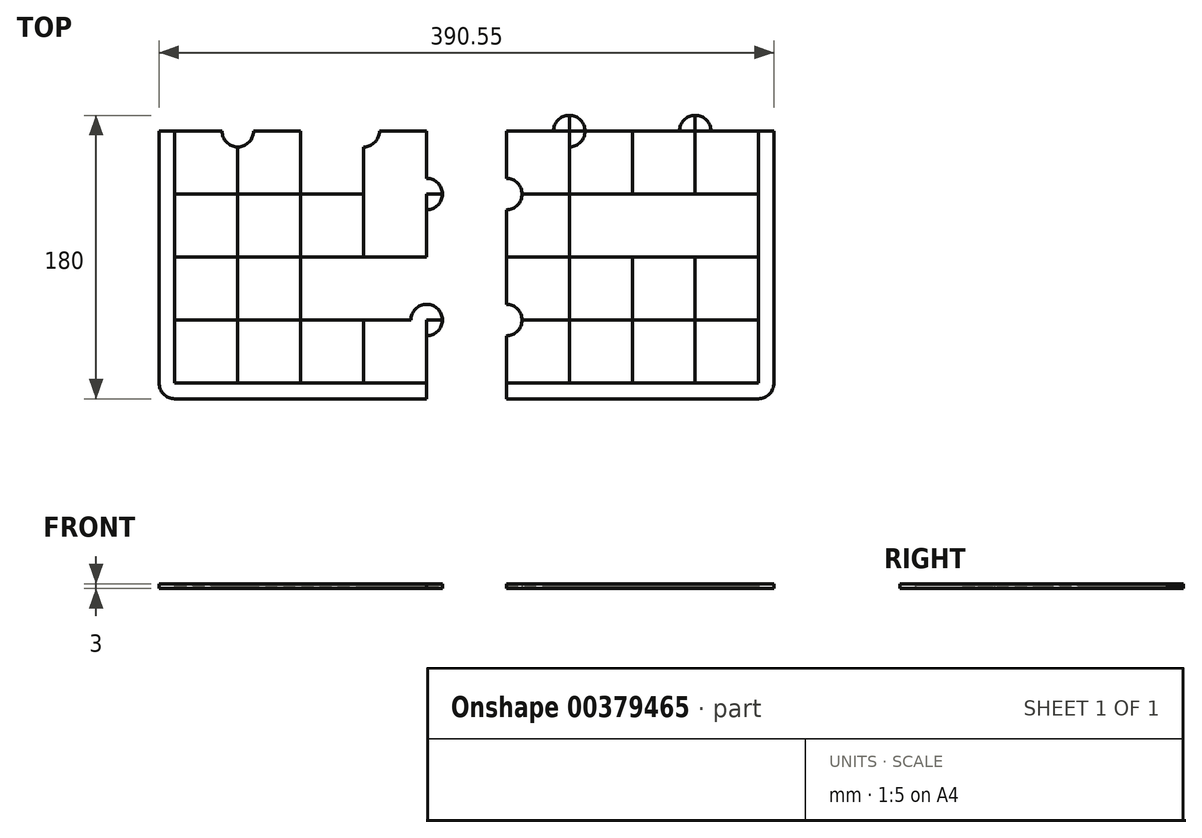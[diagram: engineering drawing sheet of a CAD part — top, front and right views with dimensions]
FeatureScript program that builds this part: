
annotation { "Feature Type Name" : "Feature", "Feature Type Description" : "" }
export const myFeature = defineFeature(function(context is Context, id is Id, definition is map)
    precondition{}
    {
        {
            var Q0;
            Q0=qCreatedBy(makeId("Top.planeOp"),FACE);
            var sketch = newSketch(context, id + "F0", { "sketchPlane" : qUnion([Q0])});
            skLineSegment(sketch, "E0.bottom", {"start": v(20, -20) * mm, "end": v(-20, -20) * mm});
            skLineSegment(sketch, "E0.top", {"start": v(20, 20) * mm, "end": v(-20, 20) * mm});
            skLineSegment(sketch, "E0.left", {"start": v(20, -20) * mm, "end": v(20, 20) * mm});
            skLineSegment(sketch, "E0.right", {"start": v(-20, -20) * mm, "end": v(-20, 20) * mm});
            skPoint(sketch, "E0.middle", {"position": v(0, 0) * mm});
            skLineSegment(sketch, "E1.bottom", {"start": v(-20, 20) * mm, "end": v(-60, 20) * mm});
            skLineSegment(sketch, "E1.top", {"start": v(-20, -20) * mm, "end": v(-60, -20) * mm});
            skLineSegment(sketch, "E1.left", {"start": v(-20, 20) * mm, "end": v(-20, -20) * mm});
            skLineSegment(sketch, "E1.right", {"start": v(-60, 20) * mm, "end": v(-60, -20) * mm});
            skLineSegment(sketch, "E2.bottom", {"start": v(20, -20) * mm, "end": v(60, -20) * mm});
            skLineSegment(sketch, "E2.top", {"start": v(20, 20) * mm, "end": v(60, 20) * mm});
            skLineSegment(sketch, "E2.right", {"start": v(60, -20) * mm, "end": v(60, 20) * mm});
            skLineSegment(sketch, "E3.bottom", {"start": v(-60, -20) * mm, "end": v(-100, -20) * mm});
            skLineSegment(sketch, "E3.top", {"start": v(-60, 20) * mm, "end": v(-100, 20) * mm});
            skLineSegment(sketch, "E3.left", {"start": v(-60, -20) * mm, "end": v(-60, 20) * mm});
            skLineSegment(sketch, "E3.right", {"start": v(-100, -20) * mm, "end": v(-100, 20) * mm});
            skLineSegment(sketch, "E4.bottom", {"start": v(-100, -20) * mm, "end": v(-60, -20) * mm});
            skLineSegment(sketch, "E4.top", {"start": v(-100, -60) * mm, "end": v(-60, -60) * mm});
            skLineSegment(sketch, "E4.left", {"start": v(-100, -20) * mm, "end": v(-100, -60) * mm});
            skLineSegment(sketch, "E4.right", {"start": v(-60, -20) * mm, "end": v(-60, -60) * mm});
            skLineSegment(sketch, "E5.top", {"start": v(-100, -100) * mm, "end": v(-60, -100) * mm});
            skLineSegment(sketch, "E5.left", {"start": v(-100, -60) * mm, "end": v(-100, -100) * mm});
            skLineSegment(sketch, "E5.right", {"start": v(-60, -60) * mm, "end": v(-60, -100) * mm});
            skPoint(sketch, "E6.oppositeSnap0", {"position": v(-60, -80) * mm});
            skLineSegment(sketch, "E6.top", {"start": v(-100, -140) * mm, "end": v(-60, -140) * mm});
            skLineSegment(sketch, "E6.left", {"start": v(-100, -100) * mm, "end": v(-100, -140) * mm});
            skLineSegment(sketch, "E6.right", {"start": v(-60, -100) * mm, "end": v(-60, -140) * mm});
            skLineSegment(sketch, "E7.bottom", {"start": v(-60, -20) * mm, "end": v(-20, -20) * mm});
            skLineSegment(sketch, "E7.top", {"start": v(-60, -60) * mm, "end": v(-20, -60) * mm});
            skLineSegment(sketch, "E7.right", {"start": v(-20, -20) * mm, "end": v(-20, -60) * mm});
            skLineSegment(sketch, "E8.bottom", {"start": v(-20, -20) * mm, "end": v(20, -20) * mm});
            skLineSegment(sketch, "E8.top", {"start": v(-20, -60) * mm, "end": v(20, -60) * mm});
            skLineSegment(sketch, "E8.right", {"start": v(20, -20) * mm, "end": v(20, -60) * mm});
            skLineSegment(sketch, "E9.top", {"start": v(20, -60) * mm, "end": v(60, -60) * mm});
            skLineSegment(sketch, "E9.right", {"start": v(60, -20) * mm, "end": v(60, -60) * mm});
            skLineSegment(sketch, "E10.bottom", {"start": v(-20, -60) * mm, "end": v(-60, -60) * mm});
            skLineSegment(sketch, "E10.top", {"start": v(-20, -100) * mm, "end": v(-60, -100) * mm});
            skLineSegment(sketch, "E10.left", {"start": v(-20, -60) * mm, "end": v(-20, -100) * mm});
            skLineSegment(sketch, "E11.bottom", {"start": v(20, -60) * mm, "end": v(-20, -60) * mm});
            skLineSegment(sketch, "E11.top", {"start": v(20, -100) * mm, "end": v(-20, -100) * mm});
            skLineSegment(sketch, "E11.left", {"start": v(20, -60) * mm, "end": v(20, -100) * mm});
            skLineSegment(sketch, "E12.bottom", {"start": v(60, -60) * mm, "end": v(20, -60) * mm});
            skLineSegment(sketch, "E12.top", {"start": v(60, -100) * mm, "end": v(20, -100) * mm});
            skLineSegment(sketch, "E12.left", {"start": v(60, -60) * mm, "end": v(60, -100) * mm});
            skLineSegment(sketch, "E13.top", {"start": v(-20, -140) * mm, "end": v(-60, -140) * mm});
            skLineSegment(sketch, "E13.left", {"start": v(-20, -100) * mm, "end": v(-20, -140) * mm});
            skLineSegment(sketch, "E14.top", {"start": v(20, -140) * mm, "end": v(-20, -140) * mm});
            skLineSegment(sketch, "E14.left", {"start": v(20, -100) * mm, "end": v(20, -140) * mm});
            skLineSegment(sketch, "E15.top", {"start": v(60, -140) * mm, "end": v(20, -140) * mm});
            skLineSegment(sketch, "E15.left", {"start": v(60, -100) * mm, "end": v(60, -140) * mm});
            skCircle(sketch, "E16", {"center": v(60, -100) * mm, "radius": 10 * mm});
            skCircle(sketch, "E17", {"center": v(60, -20) * mm, "radius": 10 * mm});
            skCircle(sketch, "E18", {"center": v(-60, 20) * mm, "radius": 10 * mm});
            skCircle(sketch, "E19", {"center": v(20, 20) * mm, "radius": 10 * mm});
            skLineSegment(sketch, "E20.bottom", {"start": v(110.55, 20) * mm, "end": v(150.55, 20) * mm});
            skLineSegment(sketch, "E20.top", {"start": v(110.55, -20) * mm, "end": v(150.55, -20) * mm});
            skLineSegment(sketch, "E20.left", {"start": v(110.55, 20) * mm, "end": v(110.55, -20) * mm});
            skLineSegment(sketch, "E20.right", {"start": v(150.55, 20) * mm, "end": v(150.55, -20) * mm});
            skLineSegment(sketch, "E21.top", {"start": v(110.55, -60) * mm, "end": v(150.55, -60) * mm});
            skLineSegment(sketch, "E21.left", {"start": v(110.55, -20) * mm, "end": v(110.55, -60) * mm});
            skLineSegment(sketch, "E21.right", {"start": v(150.55, -20) * mm, "end": v(150.55, -60) * mm});
            skLineSegment(sketch, "E22.top", {"start": v(110.55, -100) * mm, "end": v(150.55, -100) * mm});
            skLineSegment(sketch, "E22.left", {"start": v(110.55, -60) * mm, "end": v(110.55, -100) * mm});
            skLineSegment(sketch, "E22.right", {"start": v(150.55, -60) * mm, "end": v(150.55, -100) * mm});
            skLineSegment(sketch, "E23.top", {"start": v(110.55, -140) * mm, "end": v(150.55, -140) * mm});
            skLineSegment(sketch, "E23.left", {"start": v(110.55, -100) * mm, "end": v(110.55, -140) * mm});
            skLineSegment(sketch, "E23.right", {"start": v(150.55, -100) * mm, "end": v(150.55, -140) * mm});
            skLineSegment(sketch, "E24.bottom", {"start": v(150.55, 20) * mm, "end": v(190.55, 20) * mm});
            skLineSegment(sketch, "E24.top", {"start": v(150.55, -20) * mm, "end": v(190.55, -20) * mm});
            skLineSegment(sketch, "E24.right", {"start": v(190.55, 20) * mm, "end": v(190.55, -20) * mm});
            skLineSegment(sketch, "E25.bottom", {"start": v(190.55, 20) * mm, "end": v(230.55, 20) * mm});
            skLineSegment(sketch, "E25.top", {"start": v(190.55, -20) * mm, "end": v(230.55, -20) * mm});
            skLineSegment(sketch, "E25.right", {"start": v(230.55, 20) * mm, "end": v(230.55, -20) * mm});
            skLineSegment(sketch, "E26.bottom", {"start": v(230.55, 20) * mm, "end": v(270.55, 20) * mm});
            skLineSegment(sketch, "E26.top", {"start": v(230.55, -20) * mm, "end": v(270.55, -20) * mm});
            skLineSegment(sketch, "E26.right", {"start": v(270.55, 20) * mm, "end": v(270.55, -20) * mm});
            skLineSegment(sketch, "E27.bottom", {"start": v(190.55, -20) * mm, "end": v(150.55, -20) * mm});
            skLineSegment(sketch, "E27.top", {"start": v(190.55, -60) * mm, "end": v(150.55, -60) * mm});
            skLineSegment(sketch, "E27.left", {"start": v(190.55, -20) * mm, "end": v(190.55, -60) * mm});
            skLineSegment(sketch, "E28.top", {"start": v(190.55, -100) * mm, "end": v(150.55, -100) * mm});
            skLineSegment(sketch, "E28.left", {"start": v(190.55, -60) * mm, "end": v(190.55, -100) * mm});
            skLineSegment(sketch, "E29.top", {"start": v(190.55, -140) * mm, "end": v(150.55, -140) * mm});
            skLineSegment(sketch, "E29.left", {"start": v(190.55, -100) * mm, "end": v(190.55, -140) * mm});
            skLineSegment(sketch, "E30.bottom", {"start": v(230.55, -20) * mm, "end": v(190.55, -20) * mm});
            skLineSegment(sketch, "E30.top", {"start": v(230.55, -60) * mm, "end": v(190.55, -60) * mm});
            skLineSegment(sketch, "E30.left", {"start": v(230.55, -20) * mm, "end": v(230.55, -60) * mm});
            skLineSegment(sketch, "E31.top", {"start": v(230.55, -100) * mm, "end": v(190.55, -100) * mm});
            skLineSegment(sketch, "E31.left", {"start": v(230.55, -60) * mm, "end": v(230.55, -100) * mm});
            skLineSegment(sketch, "E32.top", {"start": v(230.55, -140) * mm, "end": v(190.55, -140) * mm});
            skLineSegment(sketch, "E32.left", {"start": v(230.55, -100) * mm, "end": v(230.55, -140) * mm});
            skLineSegment(sketch, "E33.bottom", {"start": v(270.55, -20) * mm, "end": v(230.55, -20) * mm});
            skLineSegment(sketch, "E33.top", {"start": v(270.55, -60) * mm, "end": v(230.55, -60) * mm});
            skLineSegment(sketch, "E33.left", {"start": v(270.55, -20) * mm, "end": v(270.55, -60) * mm});
            skLineSegment(sketch, "E34.top", {"start": v(270.55, -100) * mm, "end": v(230.55, -100) * mm});
            skLineSegment(sketch, "E34.left", {"start": v(270.55, -60) * mm, "end": v(270.55, -100) * mm});
            skLineSegment(sketch, "E35.top", {"start": v(270.55, -140) * mm, "end": v(230.55, -140) * mm});
            skLineSegment(sketch, "E35.left", {"start": v(270.55, -100) * mm, "end": v(270.55, -140) * mm});
            skCircle(sketch, "E36", {"center": v(110.55, -20) * mm, "radius": 10 * mm});
            skCircle(sketch, "E37", {"center": v(110.55, -100) * mm, "radius": 10 * mm});
            skCircle(sketch, "E38", {"center": v(150.55, 20) * mm, "radius": 10 * mm});
            skCircle(sketch, "E39", {"center": v(230.55, 20) * mm, "radius": 10 * mm});
            skLineSegment(sketch, "E40", {"start": v(-100, 20) * mm, "end": v(-110, 20) * mm});
            skLineSegment(sketch, "E41", {"start": v(60, -140) * mm, "end": v(60, -150) * mm});
            skLineSegment(sketch, "E42", {"start": v(-100, -140) * mm, "end": v(-100, -150) * mm});
            skLineSegment(sketch, "E43", {"start": v(-100, -140) * mm, "end": v(-110, -140) * mm});
            skLineSegment(sketch, "E44", {"start": v(60, -150) * mm, "end": v(-100, -150) * mm});
            skLineSegment(sketch, "E45", {"start": v(-100, -150) * mm, "end": v(-110, -140) * mm});
            skLineSegment(sketch, "E46", {"start": v(-110, 20) * mm, "end": v(-110, -140) * mm});
            skLineSegment(sketch, "E47", {"start": v(110.55, -140) * mm, "end": v(110.55, -150) * mm});
            skLineSegment(sketch, "E48", {"start": v(270.55, -140) * mm, "end": v(270.55, -150) * mm});
            skLineSegment(sketch, "E49", {"start": v(270.55, 20) * mm, "end": v(280.55, 20) * mm});
            skLineSegment(sketch, "E50", {"start": v(270.55, -140) * mm, "end": v(280.55, -140) * mm});
            skLineSegment(sketch, "E51", {"start": v(110.55, -150) * mm, "end": v(270.55, -150) * mm});
            skLineSegment(sketch, "E52", {"start": v(270.55, -150) * mm, "end": v(280.55, -140) * mm});
            skLineSegment(sketch, "E53", {"start": v(280.55, -140) * mm, "end": v(280.55, 20) * mm});
            skCircle(sketch, "E54", {"center": v(-100, -140) * mm, "radius": 10 * mm});
            skCircle(sketch, "E55", {"center": v(270.55, -140) * mm, "radius": 10 * mm});
            skLineSegment(sketch, "E56", {"start": v(60, -20) * mm, "end": v(70, -20) * mm});
            skLineSegment(sketch, "E57", {"start": v(60, -100) * mm, "end": v(70, -100) * mm});
            skLineSegment(sketch, "E58", {"start": v(20, 20) * mm, "end": v(20, 30) * mm});
            skLineSegment(sketch, "E59", {"start": v(-60, 20) * mm, "end": v(-60, 30) * mm});
            skLineSegment(sketch, "E60", {"start": v(110.55, -20) * mm, "end": v(100.55, -20) * mm});
            skLineSegment(sketch, "E61", {"start": v(150.55, 20) * mm, "end": v(150.55, 30) * mm});
            skLineSegment(sketch, "E62", {"start": v(230.55, 20) * mm, "end": v(230.55, 30) * mm});
            skLineSegment(sketch, "E63", {"start": v(110.55, -100) * mm, "end": v(100.55, -100) * mm});
            skLineSegment(sketch, "E64", {"start": v(-60, 20) * mm, "end": v(-60, 10) * mm});
            skLineSegment(sketch, "E65", {"start": v(20, 20) * mm, "end": v(20, 10) * mm});
            skLineSegment(sketch, "E66", {"start": v(-50, 20) * mm, "end": v(-60, 20) * mm});
            skLineSegment(sketch, "E67", {"start": v(-60, 20) * mm, "end": v(-70, 20) * mm});
            skLineSegment(sketch, "E68", {"start": v(30, 20) * mm, "end": v(20, 20) * mm});
            skLineSegment(sketch, "E69", {"start": v(20, 20) * mm, "end": v(10, 20) * mm});
            skSolve(sketch);
        }
        {
            var Q0;
            {var subQ1=sQuery(id+"F0.wireOp",EDGE,"E3.right");Q0=makeQuery(id+"F0.imprint","IMPRINT",FACE,{"disambiguationData":[TD([[makeQuery(id+"F0.imprint","IMPRINT",EDGE,{"derivedFrom":subQ1}),-1.0]])]});}
            var Q1;
            {var subQ1=sQuery(id+"F0.wireOp",EDGE,"E3.top");var subQ3=sQuery(id+"F0.wireOp",EDGE,"E18");var subQ4=makeQuery(id+"F0.imprint","INTERSECT",VERTEX,{"derivedFrom":[subQ1,subQ3]});Q1=makeQuery(id+"F0.imprint","IMPRINT",FACE,{"disambiguationData":[TD([[makeQuery(id+"F0.imprint","IMPRINT",EDGE,{"disambiguationData":[TD([[subQ4,-1.0]])],"derivedFrom":subQ3}),1.0]])]});}
            var Q2;
            {var subQ1=sQuery(id+"F0.wireOp",EDGE,"E1.bottom");var subQ3=sQuery(id+"F0.wireOp",EDGE,"E18");var subQ4=makeQuery(id+"F0.imprint","INTERSECT",VERTEX,{"derivedFrom":[subQ1,subQ3]});Q2=makeQuery(id+"F0.imprint","IMPRINT",FACE,{"disambiguationData":[TD([[makeQuery(id+"F0.imprint","IMPRINT",EDGE,{"disambiguationData":[TD([[subQ4,1.0]])],"derivedFrom":subQ3}),1.0]])]});}
            var Q3;
            {var subQ4=sQuery(id+"F0.wireOp",EDGE,"E1.left");Q3=makeQuery(id+"F0.imprint","IMPRINT",FACE,{"disambiguationData":[TD([[makeQuery(id+"F0.imprint","IMPRINT",EDGE,{"derivedFrom":subQ4}),-1.0]])]});}
            var Q4;
            {var subQ6=sQuery(id+"F0.wireOp",EDGE,"E1.left");Q4=makeQuery(id+"F0.imprint","IMPRINT",FACE,{"disambiguationData":[TD([[makeQuery(id+"F0.imprint","IMPRINT",EDGE,{"derivedFrom":subQ6}),1.0]])]});}
            var Q5;
            {var subQ1=sQuery(id+"F0.wireOp",EDGE,"E0.top");var subQ3=sQuery(id+"F0.wireOp",EDGE,"E19");var subQ4=makeQuery(id+"F0.imprint","INTERSECT",VERTEX,{"derivedFrom":[subQ1,subQ3]});Q5=makeQuery(id+"F0.imprint","IMPRINT",FACE,{"disambiguationData":[TD([[makeQuery(id+"F0.imprint","IMPRINT",EDGE,{"disambiguationData":[TD([[subQ4,-1.0]])],"derivedFrom":subQ3}),1.0]])]});}
            var Q6;
            {var subQ1=sQuery(id+"F0.wireOp",EDGE,"E2.top");var subQ3=sQuery(id+"F0.wireOp",EDGE,"E19");var subQ4=makeQuery(id+"F0.imprint","INTERSECT",VERTEX,{"derivedFrom":[subQ1,subQ3]});Q6=makeQuery(id+"F0.imprint","IMPRINT",FACE,{"disambiguationData":[TD([[makeQuery(id+"F0.imprint","IMPRINT",EDGE,{"disambiguationData":[TD([[subQ4,1.0]])],"derivedFrom":subQ3}),1.0]])]});}
            var Q7;
            {var subQ0=sQuery(id+"F0.wireOp",EDGE,"E2.right");var subQ1=sQuery(id+"F0.wireOp",EDGE,"E2.top");var subQ2=makeQuery(id+"F0.imprint","INTERSECT",VERTEX,{"derivedFrom":[subQ1,subQ0]});Q7=makeQuery(id+"F0.imprint","IMPRINT",FACE,{"disambiguationData":[TD([[makeQuery(id+"F0.imprint","IMPRINT",EDGE,{"disambiguationData":[TD([[subQ2,1.0]])],"derivedFrom":subQ1}),-1.0]])]});}
            var Q8;
            {var subQ1=sQuery(id+"F0.wireOp",EDGE,"E2.right");var subQ3=sQuery(id+"F0.wireOp",EDGE,"E17");var subQ4=makeQuery(id+"F0.imprint","INTERSECT",VERTEX,{"derivedFrom":[subQ1,subQ3]});Q8=makeQuery(id+"F0.imprint","IMPRINT",FACE,{"disambiguationData":[TD([[makeQuery(id+"F0.imprint","IMPRINT",EDGE,{"disambiguationData":[TD([[subQ4,-1.0]])],"derivedFrom":subQ3}),1.0]])]});}
            var Q9;
            {var subQ0=sQuery(id+"F0.wireOp",EDGE,"E9.right");var subQ3=sQuery(id+"F0.wireOp",EDGE,"E17");var subQ5=makeQuery(id+"F0.imprint","INTERSECT",VERTEX,{"derivedFrom":[subQ0,subQ3]});Q9=makeQuery(id+"F0.imprint","IMPRINT",FACE,{"disambiguationData":[TD([[makeQuery(id+"F0.imprint","IMPRINT",EDGE,{"disambiguationData":[TD([[subQ5,1.0]])],"derivedFrom":subQ3}),1.0]])]});}
            var Q10;
            {var subQ4=sQuery(id+"F0.wireOp",EDGE,"E8.right");Q10=makeQuery(id+"F0.imprint","IMPRINT",FACE,{"disambiguationData":[TD([[makeQuery(id+"F0.imprint","IMPRINT",EDGE,{"derivedFrom":subQ4}),1.0]])]});}
            var Q11;
            Q11=makeQuery(id+"F0.imprint","IMPRINT",FACE,{"disambiguationData":[TD([[makeQuery(id+"F0.imprint","IMPRINT",EDGE,{"derivedFrom":sQuery(id+"F0.wireOp",EDGE,"E8.bottom")}),-1.0]])]});
            var Q12;
            Q12=makeQuery(id+"F0.imprint","IMPRINT",FACE,{"disambiguationData":[TD([[makeQuery(id+"F0.imprint","IMPRINT",EDGE,{"derivedFrom":sQuery(id+"F0.wireOp",EDGE,"E7.bottom")}),-1.0]])]});
            var Q13;
            Q13=makeQuery(id+"F0.imprint","IMPRINT",FACE,{"disambiguationData":[TD([[makeQuery(id+"F0.imprint","IMPRINT",EDGE,{"derivedFrom":sQuery(id+"F0.wireOp",EDGE,"E4.bottom")}),-1.0]])]});
            var Q14;
            Q14=makeQuery(id+"F0.imprint","IMPRINT",FACE,{"disambiguationData":[TD([[makeQuery(id+"F0.imprint","IMPRINT",EDGE,{"derivedFrom":sQuery(id+"F0.wireOp",EDGE,"E4.top")}),-1.0]])]});
            var Q15;
            Q15=makeQuery(id+"F0.imprint","IMPRINT",FACE,{"disambiguationData":[TD([[makeQuery(id+"F0.imprint","IMPRINT",EDGE,{"derivedFrom":sQuery(id+"F0.wireOp",EDGE,"E5.top")}),-1.0]])]});
            var Q16;
            Q16=makeQuery(id+"F0.imprint","IMPRINT",FACE,{"disambiguationData":[TD([[makeQuery(id+"F0.imprint","IMPRINT",EDGE,{"derivedFrom":sQuery(id+"F0.wireOp",EDGE,"E10.top")}),1.0]])]});
            var Q17;
            Q17=makeQuery(id+"F0.imprint","IMPRINT",FACE,{"disambiguationData":[TD([[makeQuery(id+"F0.imprint","IMPRINT",EDGE,{"derivedFrom":sQuery(id+"F0.wireOp",EDGE,"E10.bottom")}),1.0]])]});
            var Q18;
            Q18=makeQuery(id+"F0.imprint","IMPRINT",FACE,{"disambiguationData":[TD([[makeQuery(id+"F0.imprint","IMPRINT",EDGE,{"derivedFrom":sQuery(id+"F0.wireOp",EDGE,"E11.bottom")}),1.0]])]});
            var Q19;
            Q19=makeQuery(id+"F0.imprint","IMPRINT",FACE,{"disambiguationData":[TD([[makeQuery(id+"F0.imprint","IMPRINT",EDGE,{"derivedFrom":sQuery(id+"F0.wireOp",EDGE,"E11.top")}),1.0]])]});
            var Q20;
            {var subQ2=sQuery(id+"F0.wireOp",EDGE,"E15.top");Q20=makeQuery(id+"F0.imprint","IMPRINT",FACE,{"disambiguationData":[TD([[makeQuery(id+"F0.imprint","IMPRINT",EDGE,{"derivedFrom":subQ2}),-1.0]])]});}
            var Q21;
            {var subQ4=sQuery(id+"F0.wireOp",EDGE,"E12.bottom");Q21=makeQuery(id+"F0.imprint","IMPRINT",FACE,{"disambiguationData":[TD([[makeQuery(id+"F0.imprint","IMPRINT",EDGE,{"derivedFrom":subQ4}),1.0]])]});}
            var Q22;
            {var subQ1=sQuery(id+"F0.wireOp",EDGE,"E12.left");var subQ3=sQuery(id+"F0.wireOp",EDGE,"E16");var subQ4=makeQuery(id+"F0.imprint","INTERSECT",VERTEX,{"derivedFrom":[subQ1,subQ3]});Q22=makeQuery(id+"F0.imprint","IMPRINT",FACE,{"disambiguationData":[TD([[makeQuery(id+"F0.imprint","IMPRINT",EDGE,{"disambiguationData":[TD([[subQ4,-1.0]])],"derivedFrom":subQ3}),1.0]])]});}
            var Q23;
            {var subQ0=sQuery(id+"F0.wireOp",EDGE,"E15.left");var subQ3=sQuery(id+"F0.wireOp",EDGE,"E16");var subQ5=makeQuery(id+"F0.imprint","INTERSECT",VERTEX,{"derivedFrom":[subQ0,subQ3]});Q23=makeQuery(id+"F0.imprint","IMPRINT",FACE,{"disambiguationData":[TD([[makeQuery(id+"F0.imprint","IMPRINT",EDGE,{"disambiguationData":[TD([[subQ5,1.0]])],"derivedFrom":subQ3}),1.0]])]});}
            var Q24;
            {var subQ1=sQuery(id+"F0.wireOp",EDGE,"E6.top");var subQ3=sQuery(id+"F0.wireOp",EDGE,"E54");var subQ4=makeQuery(id+"F0.imprint","INTERSECT",VERTEX,{"derivedFrom":[subQ1,subQ3]});Q24=makeQuery(id+"F0.imprint","IMPRINT",FACE,{"disambiguationData":[TD([[makeQuery(id+"F0.imprint","IMPRINT",EDGE,{"disambiguationData":[TD([[subQ4,-1.0]])],"derivedFrom":subQ3}),1.0]])]});}
            extrude(context, id + "F1", {"entities" : qUnion([Q0, Q1, Q2, Q3, Q4, Q5, Q6, Q7, Q8, Q9, Q10, Q11, Q12, Q13, Q14, Q15, Q16, Q17, Q18, Q19, Q20, Q21, Q22, Q23, Q24]), "depth" : 2 * mm});
        }
        {
            var Q0;
            Q0=makeQuery(id+"F1.opExtrude","CAP_FACE",FACE,{"disambiguationData":[OSD([sQuery(id+"F0.wireOp",EDGE,"E0.top"),sQuery(id+"F0.wireOp",EDGE,"E1.bottom"),sQuery(id+"F0.wireOp",EDGE,"E2.top"),sQuery(id+"F0.wireOp",EDGE,"E2.right"),sQuery(id+"F0.wireOp",EDGE,"E3.top"),sQuery(id+"F0.wireOp",EDGE,"E3.right"),sQuery(id+"F0.wireOp",EDGE,"E4.left"),sQuery(id+"F0.wireOp",EDGE,"E5.left"),sQuery(id+"F0.wireOp",EDGE,"E6.top"),sQuery(id+"F0.wireOp",EDGE,"E6.left"),sQuery(id+"F0.wireOp",EDGE,"E9.right"),sQuery(id+"F0.wireOp",EDGE,"E12.left"),sQuery(id+"F0.wireOp",EDGE,"E13.top"),sQuery(id+"F0.wireOp",EDGE,"E14.top"),sQuery(id+"F0.wireOp",EDGE,"E15.top"),sQuery(id+"F0.wireOp",EDGE,"E15.left")])],"isStart":false});
            var sketch = newSketch(context, id + "F2", { "sketchPlane" : qUnion([Q0])});
            skLineSegment(sketch, "E70.bottom", {"start": v(60, 20) * mm, "end": v(20, 20) * mm});
            skLineSegment(sketch, "E70.top", {"start": v(60, -20) * mm, "end": v(20, -20) * mm});
            skLineSegment(sketch, "E70.left", {"start": v(60, 20) * mm, "end": v(60, -20) * mm});
            skLineSegment(sketch, "E70.right", {"start": v(20, 20) * mm, "end": v(20, -20) * mm});
            skLineSegment(sketch, "E71.bottom", {"start": v(20, -20) * mm, "end": v(-20, -20) * mm});
            skLineSegment(sketch, "E71.top", {"start": v(20, 20) * mm, "end": v(-20, 20) * mm});
            skLineSegment(sketch, "E71.left", {"start": v(20, -20) * mm, "end": v(20, 20) * mm});
            skLineSegment(sketch, "E71.right", {"start": v(-20, -20) * mm, "end": v(-20, 20) * mm});
            skLineSegment(sketch, "E72.bottom", {"start": v(-20, -20) * mm, "end": v(-60, -20) * mm});
            skLineSegment(sketch, "E72.top", {"start": v(-20, 20) * mm, "end": v(-60, 20) * mm});
            skLineSegment(sketch, "E72.right", {"start": v(-60, -20) * mm, "end": v(-60, 20) * mm});
            skLineSegment(sketch, "E73.bottom", {"start": v(-60, -20) * mm, "end": v(-100, -20) * mm});
            skLineSegment(sketch, "E73.top", {"start": v(-60, 20) * mm, "end": v(-100, 20) * mm});
            skLineSegment(sketch, "E73.right", {"start": v(-100, -20) * mm, "end": v(-100, 20) * mm});
            skLineSegment(sketch, "E74.bottom", {"start": v(20, -20) * mm, "end": v(60, -20) * mm});
            skLineSegment(sketch, "E74.top", {"start": v(20, -60) * mm, "end": v(60, -60) * mm});
            skLineSegment(sketch, "E74.left", {"start": v(20, -20) * mm, "end": v(20, -60) * mm});
            skLineSegment(sketch, "E74.right", {"start": v(60, -20) * mm, "end": v(60, -60) * mm});
            skLineSegment(sketch, "E75.bottom", {"start": v(20, -60) * mm, "end": v(-20, -60) * mm});
            skLineSegment(sketch, "E75.left", {"start": v(20, -60) * mm, "end": v(20, -20) * mm});
            skLineSegment(sketch, "E75.right", {"start": v(-20, -60) * mm, "end": v(-20, -20) * mm});
            skLineSegment(sketch, "E76.bottom", {"start": v(-20, -60) * mm, "end": v(-60, -60) * mm});
            skLineSegment(sketch, "E76.right", {"start": v(-60, -60) * mm, "end": v(-60, -20) * mm});
            skLineSegment(sketch, "E77.bottom", {"start": v(-60, -60) * mm, "end": v(-100, -60) * mm});
            skLineSegment(sketch, "E77.right", {"start": v(-100, -60) * mm, "end": v(-100, -20) * mm});
            skLineSegment(sketch, "E78.bottom", {"start": v(60, -60) * mm, "end": v(20, -60) * mm});
            skLineSegment(sketch, "E78.top", {"start": v(60, -100) * mm, "end": v(20, -100) * mm});
            skLineSegment(sketch, "E78.left", {"start": v(60, -60) * mm, "end": v(60, -100) * mm});
            skLineSegment(sketch, "E78.right", {"start": v(20, -60) * mm, "end": v(20, -100) * mm});
            skLineSegment(sketch, "E79.bottom", {"start": v(20, -100) * mm, "end": v(60, -100) * mm});
            skLineSegment(sketch, "E79.top", {"start": v(20, -140) * mm, "end": v(60, -140) * mm});
            skLineSegment(sketch, "E79.left", {"start": v(20, -100) * mm, "end": v(20, -140) * mm});
            skLineSegment(sketch, "E79.right", {"start": v(60, -100) * mm, "end": v(60, -140) * mm});
            skLineSegment(sketch, "E80.bottom", {"start": v(20, -100) * mm, "end": v(-20, -100) * mm});
            skLineSegment(sketch, "E80.left", {"start": v(20, -100) * mm, "end": v(20, -60) * mm});
            skLineSegment(sketch, "E80.right", {"start": v(-20, -100) * mm, "end": v(-20, -60) * mm});
            skLineSegment(sketch, "E81.bottom", {"start": v(-20, -100) * mm, "end": v(-60, -100) * mm});
            skLineSegment(sketch, "E81.right", {"start": v(-60, -100) * mm, "end": v(-60, -60) * mm});
            skLineSegment(sketch, "E82.bottom", {"start": v(-60, -100) * mm, "end": v(-100, -100) * mm});
            skLineSegment(sketch, "E82.right", {"start": v(-100, -100) * mm, "end": v(-100, -60) * mm});
            skLineSegment(sketch, "E83.bottom", {"start": v(20, -140) * mm, "end": v(-20, -140) * mm});
            skLineSegment(sketch, "E83.left", {"start": v(20, -140) * mm, "end": v(20, -100) * mm});
            skLineSegment(sketch, "E83.right", {"start": v(-20, -140) * mm, "end": v(-20, -100) * mm});
            skLineSegment(sketch, "E84.bottom", {"start": v(-20, -140) * mm, "end": v(-60, -140) * mm});
            skLineSegment(sketch, "E84.right", {"start": v(-60, -140) * mm, "end": v(-60, -100) * mm});
            skLineSegment(sketch, "E85.bottom", {"start": v(-60, -140) * mm, "end": v(-100, -140) * mm});
            skLineSegment(sketch, "E85.right", {"start": v(-100, -140) * mm, "end": v(-100, -100) * mm});
            skCircle(sketch, "E86", {"center": v(-60, 20) * mm, "radius": 10 * mm});
            skCircle(sketch, "E87", {"center": v(20, 20) * mm, "radius": 10 * mm});
            skLineSegment(sketch, "E88", {"start": v(20, 20) * mm, "end": v(20, 30) * mm});
            skLineSegment(sketch, "E89", {"start": v(-60, 20) * mm, "end": v(-60, 30) * mm});
            skSolve(sketch);
        }
        {
            var Q0;
            {var subQ1=sQuery(id+"F0.wireOp",EDGE,"E12.left");var subQ3=sQuery(id+"F0.wireOp",EDGE,"E16");var subQ4=makeQuery(id+"F0.imprint","INTERSECT",VERTEX,{"derivedFrom":[subQ1,subQ3]});Q0=makeQuery(id+"F0.imprint","IMPRINT",FACE,{"disambiguationData":[TD([[makeQuery(id+"F0.imprint","IMPRINT",EDGE,{"disambiguationData":[TD([[subQ4,1.0]])],"derivedFrom":subQ3}),1.0]])]});}
            var Q1;
            {var subQ1=sQuery(id+"F0.wireOp",EDGE,"E2.right");var subQ3=sQuery(id+"F0.wireOp",EDGE,"E17");var subQ4=makeQuery(id+"F0.imprint","INTERSECT",VERTEX,{"derivedFrom":[subQ1,subQ3]});Q1=makeQuery(id+"F0.imprint","IMPRINT",FACE,{"disambiguationData":[TD([[makeQuery(id+"F0.imprint","IMPRINT",EDGE,{"disambiguationData":[TD([[subQ4,1.0]])],"derivedFrom":subQ3}),1.0]])]});}
            extrude(context, id + "F3", {"entities" : qUnion([Q0, Q1]), "operationType" : NewBodyOperationType.ADD, "depth" : 2 * mm});
        }
        {
            var Q0;
            {var subQ1=sQuery(id+"F0.wireOp",EDGE,"E3.top");var subQ3=sQuery(id+"F0.wireOp",EDGE,"E18");var subQ4=makeQuery(id+"F0.imprint","INTERSECT",VERTEX,{"derivedFrom":[subQ1,subQ3]});Q0=makeQuery(id+"F0.imprint","IMPRINT",FACE,{"disambiguationData":[TD([[makeQuery(id+"F0.imprint","IMPRINT",EDGE,{"disambiguationData":[TD([[subQ4,-1.0]])],"derivedFrom":subQ3}),1.0]])]});}
            var Q1;
            {var subQ1=sQuery(id+"F0.wireOp",EDGE,"E1.bottom");var subQ3=sQuery(id+"F0.wireOp",EDGE,"E18");var subQ4=makeQuery(id+"F0.imprint","INTERSECT",VERTEX,{"derivedFrom":[subQ1,subQ3]});Q1=makeQuery(id+"F0.imprint","IMPRINT",FACE,{"disambiguationData":[TD([[makeQuery(id+"F0.imprint","IMPRINT",EDGE,{"disambiguationData":[TD([[subQ4,1.0]])],"derivedFrom":subQ3}),1.0]])]});}
            var Q2;
            {var subQ1=sQuery(id+"F0.wireOp",EDGE,"E0.top");var subQ3=sQuery(id+"F0.wireOp",EDGE,"E19");var subQ4=makeQuery(id+"F0.imprint","INTERSECT",VERTEX,{"derivedFrom":[subQ1,subQ3]});Q2=makeQuery(id+"F0.imprint","IMPRINT",FACE,{"disambiguationData":[TD([[makeQuery(id+"F0.imprint","IMPRINT",EDGE,{"disambiguationData":[TD([[subQ4,-1.0]])],"derivedFrom":subQ3}),1.0]])]});}
            var Q3;
            {var subQ1=sQuery(id+"F0.wireOp",EDGE,"E2.top");var subQ3=sQuery(id+"F0.wireOp",EDGE,"E19");var subQ4=makeQuery(id+"F0.imprint","INTERSECT",VERTEX,{"derivedFrom":[subQ1,subQ3]});Q3=makeQuery(id+"F0.imprint","IMPRINT",FACE,{"disambiguationData":[TD([[makeQuery(id+"F0.imprint","IMPRINT",EDGE,{"disambiguationData":[TD([[subQ4,1.0]])],"derivedFrom":subQ3}),1.0]])]});}
            extrude(context, id + "F4", {"entities" : qUnion([Q0, Q1, Q2, Q3]), "operationType" : NewBodyOperationType.REMOVE, "depth" : 5 * mm});
        }
        {
            var Q0;
            Q0=makeQuery(id+"F2.imprint","IMPRINT",FACE,{"disambiguationData":[TD([[makeQuery(id+"F2.imprint","IMPRINT",EDGE,{"derivedFrom":sQuery(id+"F2.wireOp",EDGE,"E85.bottom")}),1.0]])]});
            var Q1;
            Q1=makeQuery(id+"F2.imprint","IMPRINT",FACE,{"disambiguationData":[TD([[makeQuery(id+"F2.imprint","IMPRINT",EDGE,{"derivedFrom":sQuery(id+"F2.wireOp",EDGE,"E83.bottom")}),1.0]])]});
            var Q2;
            Q2=makeQuery(id+"F2.imprint","IMPRINT",FACE,{"disambiguationData":[TD([[makeQuery(id+"F2.imprint","IMPRINT",EDGE,{"derivedFrom":sQuery(id+"F2.wireOp",EDGE,"E76.bottom")}),1.0]])]});
            var Q3;
            Q3=makeQuery(id+"F2.imprint","IMPRINT",FACE,{"disambiguationData":[TD([[makeQuery(id+"F2.imprint","IMPRINT",EDGE,{"derivedFrom":sQuery(id+"F2.wireOp",EDGE,"E78.bottom")}),1.0]])]});
            var Q4;
            Q4=makeQuery(id+"F2.imprint","IMPRINT",FACE,{"disambiguationData":[TD([[makeQuery(id+"F2.imprint","IMPRINT",EDGE,{"derivedFrom":sQuery(id+"F2.wireOp",EDGE,"E73.bottom")}),1.0]])]});
            var Q5;
            Q5=makeQuery(id+"F2.imprint","IMPRINT",FACE,{"disambiguationData":[TD([[makeQuery(id+"F2.imprint","IMPRINT",EDGE,{"derivedFrom":sQuery(id+"F2.wireOp",EDGE,"E71.bottom")}),1.0]])]});
            var Q6;
            {var subQ0=sQuery(id+"F2.wireOp",EDGE,"E70.left");Q6=makeQuery(id+"F2.imprint","IMPRINT",FACE,{"disambiguationData":[TD([[makeQuery(id+"F2.imprint","IMPRINT",EDGE,{"derivedFrom":subQ0}),1.0]])]});}
            var Q7;
            {var subQ1=sQuery(id+"F2.wireOp",EDGE,"E71.right");Q7=makeQuery(id+"F2.imprint","IMPRINT",FACE,{"disambiguationData":[TD([[makeQuery(id+"F2.imprint","IMPRINT",EDGE,{"derivedFrom":subQ1}),1.0]])]});}
            extrude(context, id + "F5", {"entities" : qUnion([Q0, Q1, Q2, Q3, Q4, Q5, Q6, Q7]), "depth" : 1 * mm});
        }
        {
            var Q0;
            {var subQ5=sQuery(id+"F0.wireOp",EDGE,"E23.top");Q0=makeQuery(id+"F0.imprint","IMPRINT",FACE,{"disambiguationData":[TD([[makeQuery(id+"F0.imprint","IMPRINT",EDGE,{"derivedFrom":subQ5}),1.0]])]});}
            var Q1;
            {var subQ0=sQuery(id+"F0.wireOp",EDGE,"E23.left");var subQ3=sQuery(id+"F0.wireOp",EDGE,"E37");var subQ5=makeQuery(id+"F0.imprint","INTERSECT",VERTEX,{"derivedFrom":[subQ0,subQ3]});Q1=makeQuery(id+"F0.imprint","IMPRINT",FACE,{"disambiguationData":[TD([[makeQuery(id+"F0.imprint","IMPRINT",EDGE,{"disambiguationData":[TD([[subQ5,-1.0]])],"derivedFrom":subQ3}),1.0]])]});}
            var Q2;
            {var subQ1=sQuery(id+"F0.wireOp",EDGE,"E22.left");var subQ3=sQuery(id+"F0.wireOp",EDGE,"E37");var subQ4=makeQuery(id+"F0.imprint","INTERSECT",VERTEX,{"derivedFrom":[subQ1,subQ3]});Q2=makeQuery(id+"F0.imprint","IMPRINT",FACE,{"disambiguationData":[TD([[makeQuery(id+"F0.imprint","IMPRINT",EDGE,{"disambiguationData":[TD([[subQ4,1.0]])],"derivedFrom":subQ3}),1.0]])]});}
            var Q3;
            {var subQ2=sQuery(id+"F0.wireOp",EDGE,"E21.top");Q3=makeQuery(id+"F0.imprint","IMPRINT",FACE,{"disambiguationData":[TD([[makeQuery(id+"F0.imprint","IMPRINT",EDGE,{"derivedFrom":subQ2}),-1.0]])]});}
            var Q4;
            {var subQ1=sQuery(id+"F0.wireOp",EDGE,"E21.top");Q4=makeQuery(id+"F0.imprint","IMPRINT",FACE,{"disambiguationData":[TD([[makeQuery(id+"F0.imprint","IMPRINT",EDGE,{"derivedFrom":subQ1}),1.0]])]});}
            var Q5;
            {var subQ0=sQuery(id+"F0.wireOp",EDGE,"E21.left");var subQ3=sQuery(id+"F0.wireOp",EDGE,"E36");var subQ5=makeQuery(id+"F0.imprint","INTERSECT",VERTEX,{"derivedFrom":[subQ0,subQ3]});Q5=makeQuery(id+"F0.imprint","IMPRINT",FACE,{"disambiguationData":[TD([[makeQuery(id+"F0.imprint","IMPRINT",EDGE,{"disambiguationData":[TD([[subQ5,-1.0]])],"derivedFrom":subQ3}),1.0]])]});}
            var Q6;
            {var subQ1=sQuery(id+"F0.wireOp",EDGE,"E20.left");var subQ3=sQuery(id+"F0.wireOp",EDGE,"E36");var subQ4=makeQuery(id+"F0.imprint","INTERSECT",VERTEX,{"derivedFrom":[subQ1,subQ3]});Q6=makeQuery(id+"F0.imprint","IMPRINT",FACE,{"disambiguationData":[TD([[makeQuery(id+"F0.imprint","IMPRINT",EDGE,{"disambiguationData":[TD([[subQ4,1.0]])],"derivedFrom":subQ3}),1.0]])]});}
            var Q7;
            {var subQ6=sQuery(id+"F0.wireOp",EDGE,"E20.left");var subQ9=sQuery(id+"F0.wireOp",EDGE,"E20.bottom");var subQ10=makeQuery(id+"F0.imprint","INTERSECT",VERTEX,{"derivedFrom":[subQ9,subQ6]});Q7=makeQuery(id+"F0.imprint","IMPRINT",FACE,{"disambiguationData":[TD([[makeQuery(id+"F0.imprint","IMPRINT",EDGE,{"disambiguationData":[TD([[subQ10,-1.0]])],"derivedFrom":subQ9}),-1.0]])]});}
            var Q8;
            {var subQ1=sQuery(id+"F0.wireOp",EDGE,"E20.bottom");var subQ3=sQuery(id+"F0.wireOp",EDGE,"E38");var subQ4=makeQuery(id+"F0.imprint","INTERSECT",VERTEX,{"derivedFrom":[subQ1,subQ3]});Q8=makeQuery(id+"F0.imprint","IMPRINT",FACE,{"disambiguationData":[TD([[makeQuery(id+"F0.imprint","IMPRINT",EDGE,{"disambiguationData":[TD([[subQ4,-1.0]])],"derivedFrom":subQ3}),1.0]])]});}
            var Q9;
            {var subQ1=sQuery(id+"F0.wireOp",EDGE,"E24.bottom");var subQ3=sQuery(id+"F0.wireOp",EDGE,"E38");var subQ4=makeQuery(id+"F0.imprint","INTERSECT",VERTEX,{"derivedFrom":[subQ1,subQ3]});Q9=makeQuery(id+"F0.imprint","IMPRINT",FACE,{"disambiguationData":[TD([[makeQuery(id+"F0.imprint","IMPRINT",EDGE,{"disambiguationData":[TD([[subQ4,1.0]])],"derivedFrom":subQ3}),1.0]])]});}
            var Q10;
            {var subQ1=sQuery(id+"F0.wireOp",EDGE,"E24.right");Q10=makeQuery(id+"F0.imprint","IMPRINT",FACE,{"disambiguationData":[TD([[makeQuery(id+"F0.imprint","IMPRINT",EDGE,{"derivedFrom":subQ1}),-1.0]])]});}
            var Q11;
            {var subQ4=sQuery(id+"F0.wireOp",EDGE,"E24.right");Q11=makeQuery(id+"F0.imprint","IMPRINT",FACE,{"disambiguationData":[TD([[makeQuery(id+"F0.imprint","IMPRINT",EDGE,{"derivedFrom":subQ4}),1.0]])]});}
            var Q12;
            {var subQ1=sQuery(id+"F0.wireOp",EDGE,"E25.bottom");var subQ3=sQuery(id+"F0.wireOp",EDGE,"E39");var subQ4=makeQuery(id+"F0.imprint","INTERSECT",VERTEX,{"derivedFrom":[subQ1,subQ3]});Q12=makeQuery(id+"F0.imprint","IMPRINT",FACE,{"disambiguationData":[TD([[makeQuery(id+"F0.imprint","IMPRINT",EDGE,{"disambiguationData":[TD([[subQ4,-1.0]])],"derivedFrom":subQ3}),1.0]])]});}
            var Q13;
            {var subQ1=sQuery(id+"F0.wireOp",EDGE,"E26.bottom");var subQ3=sQuery(id+"F0.wireOp",EDGE,"E39");var subQ4=makeQuery(id+"F0.imprint","INTERSECT",VERTEX,{"derivedFrom":[subQ1,subQ3]});Q13=makeQuery(id+"F0.imprint","IMPRINT",FACE,{"disambiguationData":[TD([[makeQuery(id+"F0.imprint","IMPRINT",EDGE,{"disambiguationData":[TD([[subQ4,1.0]])],"derivedFrom":subQ3}),1.0]])]});}
            var Q14;
            {var subQ1=sQuery(id+"F0.wireOp",EDGE,"E26.right");Q14=makeQuery(id+"F0.imprint","IMPRINT",FACE,{"disambiguationData":[TD([[makeQuery(id+"F0.imprint","IMPRINT",EDGE,{"derivedFrom":subQ1}),-1.0]])]});}
            var Q15;
            Q15=makeQuery(id+"F0.imprint","IMPRINT",FACE,{"disambiguationData":[TD([[makeQuery(id+"F0.imprint","IMPRINT",EDGE,{"derivedFrom":sQuery(id+"F0.wireOp",EDGE,"E33.bottom")}),1.0]])]});
            var Q16;
            Q16=makeQuery(id+"F0.imprint","IMPRINT",FACE,{"disambiguationData":[TD([[makeQuery(id+"F0.imprint","IMPRINT",EDGE,{"derivedFrom":sQuery(id+"F0.wireOp",EDGE,"E30.bottom")}),1.0]])]});
            var Q17;
            Q17=makeQuery(id+"F0.imprint","IMPRINT",FACE,{"disambiguationData":[TD([[makeQuery(id+"F0.imprint","IMPRINT",EDGE,{"derivedFrom":sQuery(id+"F0.wireOp",EDGE,"E27.bottom")}),1.0]])]});
            var Q18;
            Q18=makeQuery(id+"F0.imprint","IMPRINT",FACE,{"disambiguationData":[TD([[makeQuery(id+"F0.imprint","IMPRINT",EDGE,{"derivedFrom":sQuery(id+"F0.wireOp",EDGE,"E27.top")}),1.0]])]});
            var Q19;
            Q19=makeQuery(id+"F0.imprint","IMPRINT",FACE,{"disambiguationData":[TD([[makeQuery(id+"F0.imprint","IMPRINT",EDGE,{"derivedFrom":sQuery(id+"F0.wireOp",EDGE,"E30.top")}),1.0]])]});
            var Q20;
            Q20=makeQuery(id+"F0.imprint","IMPRINT",FACE,{"disambiguationData":[TD([[makeQuery(id+"F0.imprint","IMPRINT",EDGE,{"derivedFrom":sQuery(id+"F0.wireOp",EDGE,"E33.top")}),1.0]])]});
            var Q21;
            Q21=makeQuery(id+"F0.imprint","IMPRINT",FACE,{"disambiguationData":[TD([[makeQuery(id+"F0.imprint","IMPRINT",EDGE,{"derivedFrom":sQuery(id+"F0.wireOp",EDGE,"E34.top")}),1.0]])]});
            var Q22;
            Q22=makeQuery(id+"F0.imprint","IMPRINT",FACE,{"disambiguationData":[TD([[makeQuery(id+"F0.imprint","IMPRINT",EDGE,{"derivedFrom":sQuery(id+"F0.wireOp",EDGE,"E31.top")}),1.0]])]});
            var Q23;
            Q23=makeQuery(id+"F0.imprint","IMPRINT",FACE,{"disambiguationData":[TD([[makeQuery(id+"F0.imprint","IMPRINT",EDGE,{"derivedFrom":sQuery(id+"F0.wireOp",EDGE,"E28.top")}),1.0]])]});
            var Q24;
            {var subQ1=sQuery(id+"F0.wireOp",EDGE,"E35.top");var subQ3=sQuery(id+"F0.wireOp",EDGE,"E55");var subQ4=makeQuery(id+"F0.imprint","INTERSECT",VERTEX,{"derivedFrom":[subQ1,subQ3]});Q24=makeQuery(id+"F0.imprint","IMPRINT",FACE,{"disambiguationData":[TD([[makeQuery(id+"F0.imprint","IMPRINT",EDGE,{"disambiguationData":[TD([[subQ4,1.0]])],"derivedFrom":subQ3}),1.0]])]});}
            extrude(context, id + "F6", {"entities" : qUnion([Q0, Q1, Q2, Q3, Q4, Q5, Q6, Q7, Q8, Q9, Q10, Q11, Q12, Q13, Q14, Q15, Q16, Q17, Q18, Q19, Q20, Q21, Q22, Q23, Q24]), "depth" : 2 * mm});
        }
        {
            var Q0;
            {var subQ1=sQuery(id+"F0.wireOp",EDGE,"E20.bottom");var subQ3=sQuery(id+"F0.wireOp",EDGE,"E38");var subQ4=makeQuery(id+"F0.imprint","INTERSECT",VERTEX,{"derivedFrom":[subQ1,subQ3]});Q0=makeQuery(id+"F0.imprint","IMPRINT",FACE,{"disambiguationData":[TD([[makeQuery(id+"F0.imprint","IMPRINT",EDGE,{"disambiguationData":[TD([[subQ4,1.0]])],"derivedFrom":subQ3}),1.0]])]});}
            var Q1;
            {var subQ1=sQuery(id+"F0.wireOp",EDGE,"E25.bottom");var subQ3=sQuery(id+"F0.wireOp",EDGE,"E39");var subQ4=makeQuery(id+"F0.imprint","INTERSECT",VERTEX,{"derivedFrom":[subQ1,subQ3]});Q1=makeQuery(id+"F0.imprint","IMPRINT",FACE,{"disambiguationData":[TD([[makeQuery(id+"F0.imprint","IMPRINT",EDGE,{"disambiguationData":[TD([[subQ4,1.0]])],"derivedFrom":subQ3}),1.0]])]});}
            extrude(context, id + "F7", {"entities" : qUnion([Q0, Q1]), "operationType" : NewBodyOperationType.ADD, "depth" : 3 * mm, "offsetDistance" : 25 * mm});
        }
        {
            var Q0;
            {var subQ1=sQuery(id+"F0.wireOp",EDGE,"E22.left");var subQ3=sQuery(id+"F0.wireOp",EDGE,"E37");var subQ4=makeQuery(id+"F0.imprint","INTERSECT",VERTEX,{"derivedFrom":[subQ1,subQ3]});Q0=makeQuery(id+"F0.imprint","IMPRINT",FACE,{"disambiguationData":[TD([[makeQuery(id+"F0.imprint","IMPRINT",EDGE,{"disambiguationData":[TD([[subQ4,1.0]])],"derivedFrom":subQ3}),1.0]])]});}
            var Q1;
            {var subQ0=sQuery(id+"F0.wireOp",EDGE,"E23.left");var subQ3=sQuery(id+"F0.wireOp",EDGE,"E37");var subQ5=makeQuery(id+"F0.imprint","INTERSECT",VERTEX,{"derivedFrom":[subQ0,subQ3]});Q1=makeQuery(id+"F0.imprint","IMPRINT",FACE,{"disambiguationData":[TD([[makeQuery(id+"F0.imprint","IMPRINT",EDGE,{"disambiguationData":[TD([[subQ5,-1.0]])],"derivedFrom":subQ3}),1.0]])]});}
            var Q2;
            {var subQ1=sQuery(id+"F0.wireOp",EDGE,"E20.left");var subQ3=sQuery(id+"F0.wireOp",EDGE,"E36");var subQ4=makeQuery(id+"F0.imprint","INTERSECT",VERTEX,{"derivedFrom":[subQ1,subQ3]});Q2=makeQuery(id+"F0.imprint","IMPRINT",FACE,{"disambiguationData":[TD([[makeQuery(id+"F0.imprint","IMPRINT",EDGE,{"disambiguationData":[TD([[subQ4,1.0]])],"derivedFrom":subQ3}),1.0]])]});}
            var Q3;
            {var subQ0=sQuery(id+"F0.wireOp",EDGE,"E21.left");var subQ3=sQuery(id+"F0.wireOp",EDGE,"E36");var subQ5=makeQuery(id+"F0.imprint","INTERSECT",VERTEX,{"derivedFrom":[subQ0,subQ3]});Q3=makeQuery(id+"F0.imprint","IMPRINT",FACE,{"disambiguationData":[TD([[makeQuery(id+"F0.imprint","IMPRINT",EDGE,{"disambiguationData":[TD([[subQ5,-1.0]])],"derivedFrom":subQ3}),1.0]])]});}
            extrude(context, id + "F8", {"entities" : qUnion([Q0, Q1, Q2, Q3]), "operationType" : NewBodyOperationType.REMOVE, "depth" : 4 * mm});
        }
        {
            var Q0;
            Q0=makeQuery(id+"F0.imprint","IMPRINT",FACE,{"disambiguationData":[TD([[makeQuery(id+"F0.imprint","IMPRINT",EDGE,{"derivedFrom":sQuery(id+"F0.wireOp",EDGE,"E3.right")}),1.0]])]});
            var Q1;
            Q1=makeQuery(id+"F0.imprint","IMPRINT",FACE,{"disambiguationData":[TD([[makeQuery(id+"F0.imprint","IMPRINT",EDGE,{"derivedFrom":sQuery(id+"F0.wireOp",EDGE,"E42")}),-1.0]])]});
            var Q2;
            Q2=makeQuery(id+"F0.imprint","IMPRINT",FACE,{"disambiguationData":[TD([[makeQuery(id+"F0.imprint","IMPRINT",EDGE,{"derivedFrom":sQuery(id+"F0.wireOp",EDGE,"E6.top")}),-1.0]])]});
            var Q3;
            Q3=makeQuery(id+"F0.imprint","IMPRINT",FACE,{"disambiguationData":[TD([[makeQuery(id+"F0.imprint","IMPRINT",EDGE,{"derivedFrom":sQuery(id+"F0.wireOp",EDGE,"E23.top")}),-1.0]])]});
            var Q4;
            Q4=makeQuery(id+"F0.imprint","IMPRINT",FACE,{"disambiguationData":[TD([[makeQuery(id+"F0.imprint","IMPRINT",EDGE,{"derivedFrom":sQuery(id+"F0.wireOp",EDGE,"E48")}),1.0]])]});
            var Q5;
            Q5=makeQuery(id+"F0.imprint","IMPRINT",FACE,{"disambiguationData":[TD([[makeQuery(id+"F0.imprint","IMPRINT",EDGE,{"derivedFrom":sQuery(id+"F0.wireOp",EDGE,"E26.right")}),1.0]])]});
            var Q6;
            {var subQ0=sQuery(id+"F0.wireOp",EDGE,"E43");Q6=makeQuery(id+"F0.imprint","IMPRINT",FACE,{"disambiguationData":[TD([[makeQuery(id+"F0.imprint","IMPRINT",EDGE,{"derivedFrom":subQ0}),-1.0]])]});}
            var Q7;
            {var subQ4=sQuery(id+"F0.wireOp",EDGE,"E13.top");Q7=makeQuery(id+"F0.imprint","IMPRINT",FACE,{"disambiguationData":[TD([[makeQuery(id+"F0.imprint","IMPRINT",EDGE,{"derivedFrom":subQ4}),1.0]])]});}
            var Q8;
            {var subQ0=sQuery(id+"F0.wireOp",EDGE,"E45");Q8=makeQuery(id+"F0.imprint","IMPRINT",FACE,{"disambiguationData":[TD([[makeQuery(id+"F0.imprint","IMPRINT",EDGE,{"derivedFrom":subQ0}),1.0]])]});}
            var Q9;
            {var subQ0=sQuery(id+"F0.wireOp",EDGE,"E48");Q9=makeQuery(id+"F0.imprint","IMPRINT",FACE,{"disambiguationData":[TD([[makeQuery(id+"F0.imprint","IMPRINT",EDGE,{"derivedFrom":subQ0}),-1.0]])]});}
            var Q10;
            {var subQ0=sQuery(id+"F0.wireOp",EDGE,"E50");Q10=makeQuery(id+"F0.imprint","IMPRINT",FACE,{"disambiguationData":[TD([[makeQuery(id+"F0.imprint","IMPRINT",EDGE,{"derivedFrom":subQ0}),1.0]])]});}
            var Q11;
            {var subQ0=sQuery(id+"F0.wireOp",EDGE,"E52");Q11=makeQuery(id+"F0.imprint","IMPRINT",FACE,{"disambiguationData":[TD([[makeQuery(id+"F0.imprint","IMPRINT",EDGE,{"derivedFrom":subQ0}),-1.0]])]});}
            extrude(context, id + "F9", {"entities" : qUnion([Q0, Q1, Q2, Q3, Q4, Q5, Q6, Q7, Q8, Q9, Q10, Q11]), "depth" : 3 * mm});
        }
        {
            var Q0;
            {var subQ0=sQuery(id+"F0.wireOp",EDGE,"E57");Q0=makeQuery(id+"F0.imprint","IMPRINT",FACE,{"disambiguationData":[TD([[makeQuery(id+"F0.imprint","IMPRINT",EDGE,{"derivedFrom":subQ0}),-1.0]])]});}
            var Q1;
            {var subQ0=sQuery(id+"F0.wireOp",EDGE,"E56");Q1=makeQuery(id+"F0.imprint","IMPRINT",FACE,{"disambiguationData":[TD([[makeQuery(id+"F0.imprint","IMPRINT",EDGE,{"derivedFrom":subQ0}),-1.0]])]});}
            extrude(context, id + "F10", {"entities" : qUnion([Q0, Q1]), "operationType" : NewBodyOperationType.ADD, "depth" : 3 * mm});
        }
        {
            var Q0;
            {var subQ1=sQuery(id+"F0.wireOp",EDGE,"E21.top");Q0=makeQuery(id+"F0.imprint","IMPRINT",FACE,{"disambiguationData":[TD([[makeQuery(id+"F0.imprint","IMPRINT",EDGE,{"derivedFrom":subQ1}),1.0]])]});}
            var Q1;
            {var subQ5=sQuery(id+"F0.wireOp",EDGE,"E23.top");Q1=makeQuery(id+"F0.imprint","IMPRINT",FACE,{"disambiguationData":[TD([[makeQuery(id+"F0.imprint","IMPRINT",EDGE,{"derivedFrom":subQ5}),1.0]])]});}
            var Q2;
            Q2=makeQuery(id+"F0.imprint","IMPRINT",FACE,{"disambiguationData":[TD([[makeQuery(id+"F0.imprint","IMPRINT",EDGE,{"derivedFrom":sQuery(id+"F0.wireOp",EDGE,"E27.top")}),1.0]])]});
            var Q3;
            {var subQ1=sQuery(id+"F0.wireOp",EDGE,"E24.right");Q3=makeQuery(id+"F0.imprint","IMPRINT",FACE,{"disambiguationData":[TD([[makeQuery(id+"F0.imprint","IMPRINT",EDGE,{"derivedFrom":subQ1}),-1.0]])]});}
            var Q4;
            Q4=makeQuery(id+"F0.imprint","IMPRINT",FACE,{"disambiguationData":[TD([[makeQuery(id+"F0.imprint","IMPRINT",EDGE,{"derivedFrom":sQuery(id+"F0.wireOp",EDGE,"E30.bottom")}),1.0]])]});
            var Q5;
            Q5=makeQuery(id+"F0.imprint","IMPRINT",FACE,{"disambiguationData":[TD([[makeQuery(id+"F0.imprint","IMPRINT",EDGE,{"derivedFrom":sQuery(id+"F0.wireOp",EDGE,"E31.top")}),1.0]])]});
            var Q6;
            Q6=makeQuery(id+"F0.imprint","IMPRINT",FACE,{"disambiguationData":[TD([[makeQuery(id+"F0.imprint","IMPRINT",EDGE,{"derivedFrom":sQuery(id+"F0.wireOp",EDGE,"E33.top")}),1.0]])]});
            var Q7;
            {var subQ1=sQuery(id+"F0.wireOp",EDGE,"E26.right");Q7=makeQuery(id+"F0.imprint","IMPRINT",FACE,{"disambiguationData":[TD([[makeQuery(id+"F0.imprint","IMPRINT",EDGE,{"derivedFrom":subQ1}),-1.0]])]});}
            var Q8;
            {var subQ1=sQuery(id+"F0.wireOp",EDGE,"E24.bottom");var subQ3=sQuery(id+"F0.wireOp",EDGE,"E38");var subQ4=makeQuery(id+"F0.imprint","INTERSECT",VERTEX,{"derivedFrom":[subQ1,subQ3]});Q8=makeQuery(id+"F0.imprint","IMPRINT",FACE,{"disambiguationData":[TD([[makeQuery(id+"F0.imprint","IMPRINT",EDGE,{"disambiguationData":[TD([[subQ4,1.0]])],"derivedFrom":subQ3}),1.0]])]});}
            var Q9;
            {var subQ1=sQuery(id+"F0.wireOp",EDGE,"E26.bottom");var subQ3=sQuery(id+"F0.wireOp",EDGE,"E39");var subQ4=makeQuery(id+"F0.imprint","INTERSECT",VERTEX,{"derivedFrom":[subQ1,subQ3]});Q9=makeQuery(id+"F0.imprint","IMPRINT",FACE,{"disambiguationData":[TD([[makeQuery(id+"F0.imprint","IMPRINT",EDGE,{"disambiguationData":[TD([[subQ4,1.0]])],"derivedFrom":subQ3}),1.0]])]});}
            extrude(context, id + "F11", {"entities" : qUnion([Q0, Q1, Q2, Q3, Q4, Q5, Q6, Q7, Q8, Q9]), "depth" : 3 * mm, "offsetDistance" : 25 * mm});
        }
        {
            var Q0;
            {var subQ0=sQuery(id+"F0.wireOp",EDGE,"E61");Q0=makeQuery(id+"F0.imprint","IMPRINT",FACE,{"disambiguationData":[TD([[makeQuery(id+"F0.imprint","IMPRINT",EDGE,{"derivedFrom":subQ0}),-1.0]])]});}
            var Q1;
            {var subQ0=sQuery(id+"F0.wireOp",EDGE,"E62");Q1=makeQuery(id+"F0.imprint","IMPRINT",FACE,{"disambiguationData":[TD([[makeQuery(id+"F0.imprint","IMPRINT",EDGE,{"derivedFrom":subQ0}),-1.0]])]});}
            extrude(context, id + "F12", {"entities" : qUnion([Q0, Q1]), "depth" : 2 * mm, "offsetDistance" : 25 * mm});
        }
    });
